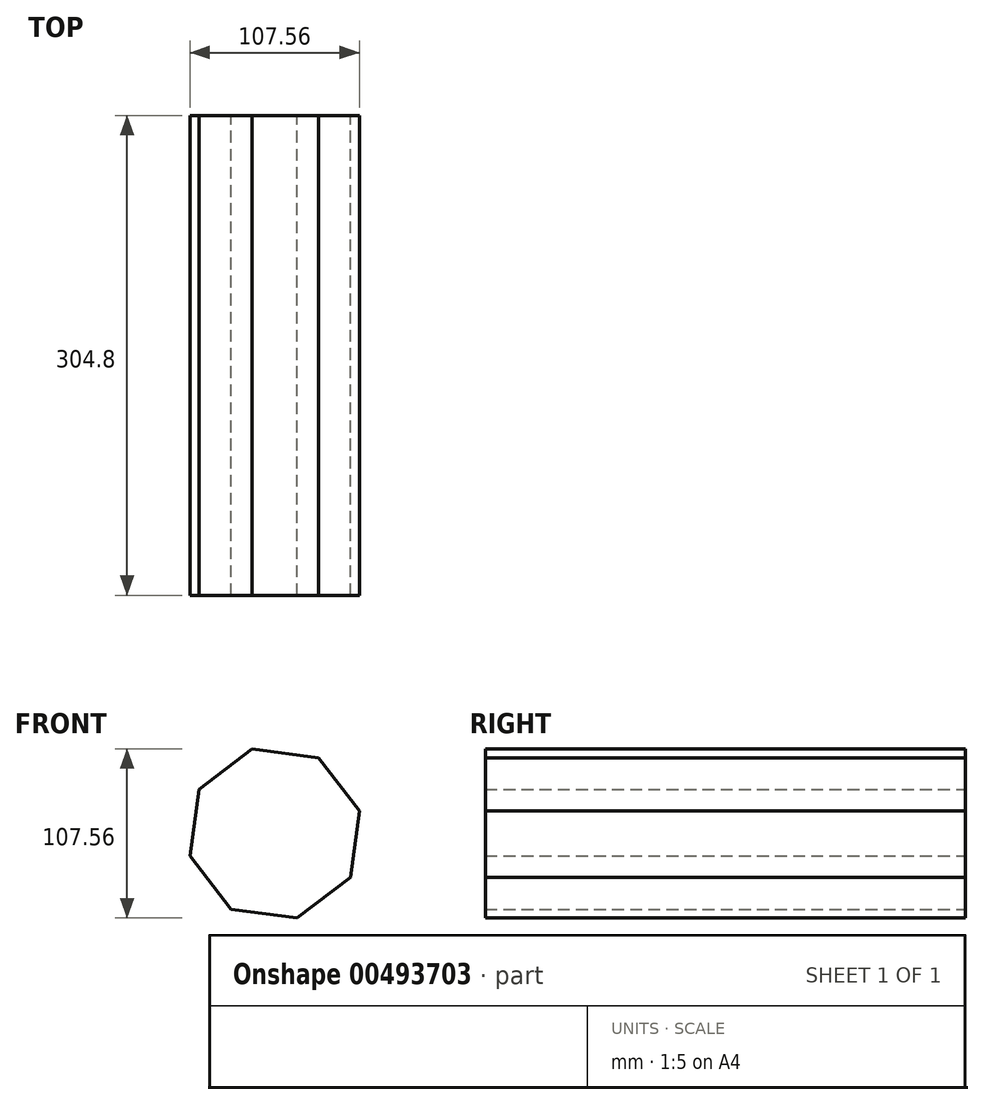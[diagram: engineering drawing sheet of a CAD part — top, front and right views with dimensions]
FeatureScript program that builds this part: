
annotation { "Feature Type Name" : "Feature", "Feature Type Description" : "" }
export const myFeature = defineFeature(function(context is Context, id is Id, definition is map)
    precondition{}
    {
        {
            var Q0;
            Q0=qCreatedBy(makeId("Front.planeOp"),FACE);
            var sketch = newSketch(context, id + "F0", { "sketchPlane" : qUnion([Q0])});
            skCircle(sketch, "E0.cCircle", {"center": v(0, 0) * mm, "radius": 55.64 * mm, "construction": true});
            skLineSegment(sketch, "E0.0", {"start": v(-14.28, 53.78) * mm, "end": v(27.93, 48.13) * mm});
            skLineSegment(sketch, "E0.1", {"start": v(27.93, 48.13) * mm, "end": v(53.78, 14.28) * mm});
            skLineSegment(sketch, "E0.2", {"start": v(53.78, 14.28) * mm, "end": v(48.13, -27.93) * mm});
            skLineSegment(sketch, "E0.3", {"start": v(48.13, -27.93) * mm, "end": v(14.28, -53.78) * mm});
            skLineSegment(sketch, "E0.4", {"start": v(14.28, -53.78) * mm, "end": v(-27.93, -48.13) * mm});
            skLineSegment(sketch, "E0.5", {"start": v(-27.93, -48.13) * mm, "end": v(-53.78, -14.28) * mm});
            skLineSegment(sketch, "E0.6", {"start": v(-53.78, -14.28) * mm, "end": v(-48.13, 27.93) * mm});
            skLineSegment(sketch, "E0.7", {"start": v(-48.13, 27.93) * mm, "end": v(-14.28, 53.78) * mm});
            skSolve(sketch);
        }
        {
            var Q0;
            Q0=makeQuery(id+"F0.imprint","IMPRINT",FACE,{"disambiguationData":[TD([[makeQuery(id+"F0.imprint","IMPRINT",EDGE,{"derivedFrom":sQuery(id+"F0.wireOp",EDGE,"E0.0")}),-1.0]])]});
            extrude(context, id + "F1", {"entities" : qUnion([Q0]), "depth" : 304.8 * mm});
        }
    });
